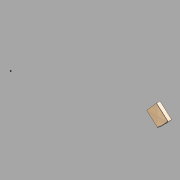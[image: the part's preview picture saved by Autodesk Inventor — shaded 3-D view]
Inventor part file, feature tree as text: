
AUTODESK INVENTOR PART (.ipt)
format: ipt  version: 2022.1 (Build 261234020, 234B)  size: 159,232 bytes
history: native  units: in
note: dims shown in document units (in); Inventor stores cm internally (conversion verified against a paired STEP export)
features: sketch x6, other x3, plane x2
ambient origin geometry x8: Origin, YZ Plane, XZ Plane, XY Plane, X Axis, Y Axis, Z Axis, Center Point
bodies: Solid1 (feature_tree)
feature tree (11):
  other  "Solid18.ipt"
  other  "Solid1::Solid18.ipt"
  other  "TaggingFeature1"
  sketch  "Sketch1"  dims[d0=0.3937in]
  sketch  "Sketch2"
  sketch  "Sketch3"
  sketch  "Sketch4"
  sketch  "Sketch5"
  sketch  "Sketch6"
  plane  "Work Plane1"
  plane  "Work Plane2"
